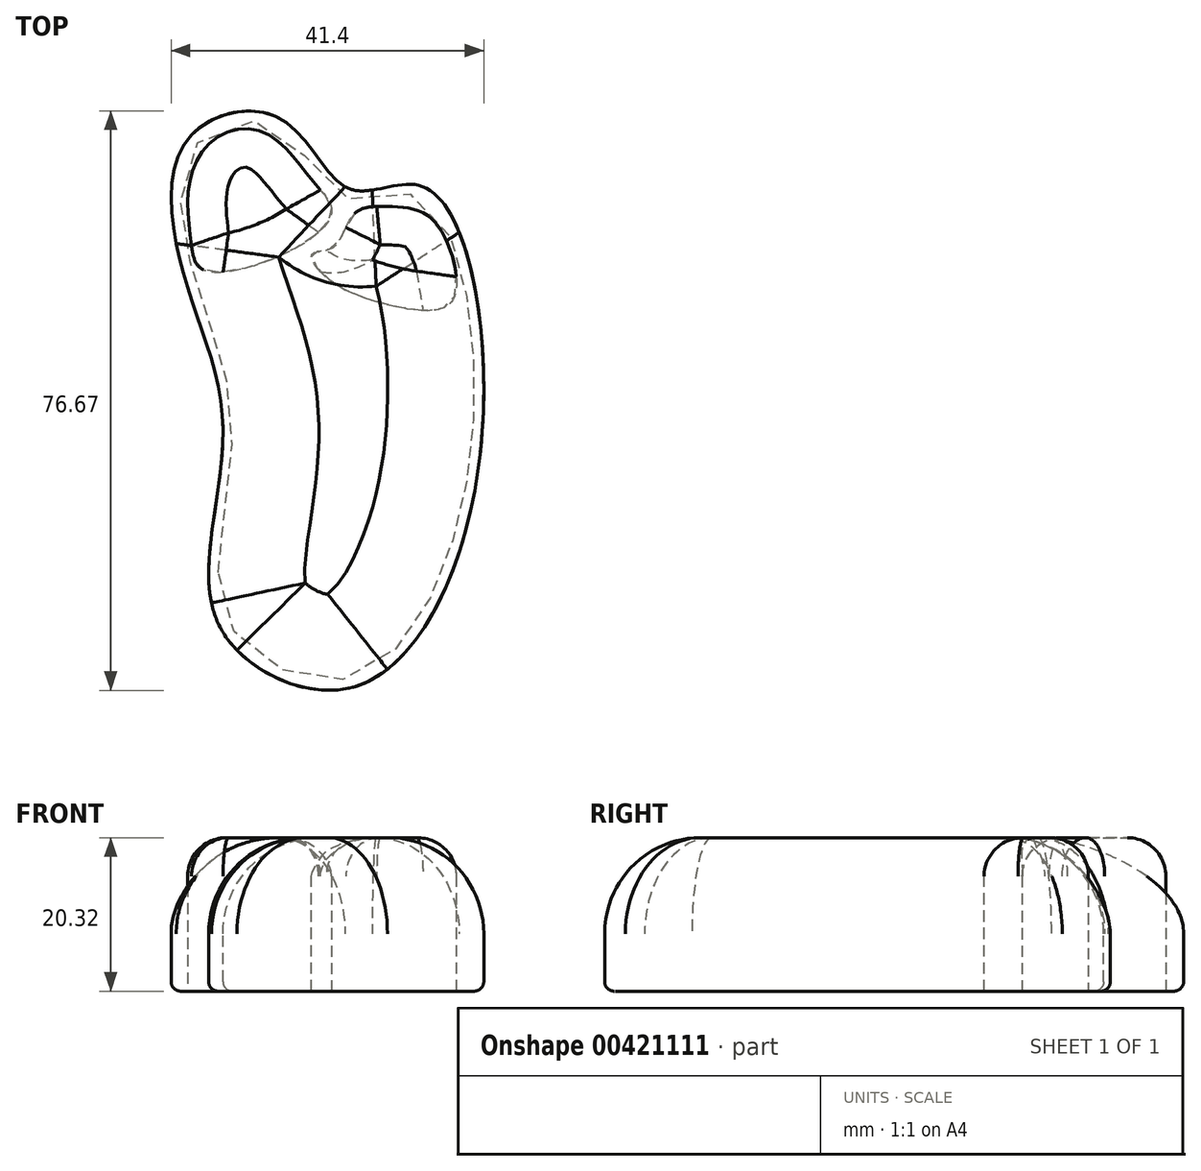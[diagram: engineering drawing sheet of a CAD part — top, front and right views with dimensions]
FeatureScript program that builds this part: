
annotation { "Feature Type Name" : "Feature", "Feature Type Description" : "" }
export const myFeature = defineFeature(function(context is Context, id is Id, definition is map)
    precondition{}
    {
        {
            var Q0;
            Q0=qCreatedBy(makeId("Top.planeOp"),FACE);
            var sketch = newSketch(context, id + "F0", { "sketchPlane" : qUnion([Q0])});
            skFitSpline(sketch, "E0", {"points": [v(-13.72, -25.12) * mm, v(-9.37, -36.03) * mm, v(6.49, -40) * mm, v(22.33, -8.6) * mm, v(14.89, 25.82) * mm, v(5.04, 25.58) * mm, v(-4.19, 34.89) * mm, v(-16.57, 32.07) * mm, v(-16.98, 14.19) * mm, v(-11.86, -4.88) * mm, v(-13.72, -25.12) * mm]});
            skSolve(sketch);
        }
        {
            var Q0;
            Q0=makeQuery(id+"F0.imprint","IMPRINT",FACE,{"disambiguationData":[TD([[makeQuery(id+"F0.imprint","IMPRINT",EDGE,{"derivedFrom":sQuery(id+"F0.wireOp",EDGE,"E0")}),1.0]])]});
            extrude(context, id + "F1", {"entities" : qUnion([Q0]), "depth" : 20.32 * mm});
        }
        {
            var Q0;
            Q0=makeQuery(id+"F1.opExtrude","CAP_EDGE",EDGE,{"disambiguationData":[OSD([sQuery(id+"F0.wireOp",EDGE,"E0")])],"isStart":false});
            fillet(context, id + "F2", {"entities" : qUnion([Q0]), "radius" : 12.7 * mm, "tangentPropagation" : true, "allowEdgeOverflow" : false});
        }
        {
            var Q0;
            Q0=makeQuery(id+"F1.opExtrude","CAP_EDGE",EDGE,{"disambiguationData":[OSD([sQuery(id+"F0.wireOp",EDGE,"E0")])],"isStart":true});
            fillet(context, id + "F3", {"entities" : qUnion([Q0]), "radius" : 1.27 * mm, "tangentPropagation" : true, "allowEdgeOverflow" : false});
        }
        {
            var Q0;
            Q0=qCreatedBy(makeId("Top.planeOp"),FACE);
            var sketch = newSketch(context, id + "F4", { "sketchPlane" : qUnion([Q0])});
            skFitSpline(sketch, "E1", {"points": [v(-14.42, 14.89) * mm, v(-16.05, 18.6) * mm, v(-16.28, 26.28) * mm, v(-12.8, 32.33) * mm, v(-6.28, 33.03) * mm, v(0, 26.75) * mm, v(2.56, 22.56) * mm, v(-3.26, 17.21) * mm, v(-14.42, 14.89) * mm]});
            skFitSpline(sketch, "E2", {"points": [v(5.58, 22.33) * mm, v(2.8, 17.9) * mm, v(0, 16.98) * mm, v(2.1, 13.72) * mm, v(11.4, 10) * mm, v(18.6, 10.93) * mm, v(16.28, 21.17) * mm, v(10.7, 23.26) * mm, v(5.58, 22.33) * mm]});
            skSolve(sketch);
        }
        {
            var Q0;
            Q0 = qSketchRegion(id + "F4", true);
            var Q1;
            Q1=sQuery(id+"F4.wireOp",EDGE,"E1");
            var Q2;
            Q2=sQuery(id+"F4.wireOp",EDGE,"E2");
            extrude(context, id + "F5", {"entities" : qUnion([Q0]), "surfaceEntities" : qUnion([Q1, Q2]), "depth" : 20.32 * mm});
        }
        {
            var Q0;
            Q0=makeQuery(id+"F5.opExtrude","CAP_EDGE",EDGE,{"disambiguationData":[OSD([sQuery(id+"F4.wireOp",EDGE,"E2")])],"isStart":false});
            var Q1;
            Q1=makeQuery(id+"F5.opExtrude","CAP_EDGE",EDGE,{"disambiguationData":[OSD([sQuery(id+"F4.wireOp",EDGE,"E1")])],"isStart":false});
            fillet(context, id + "F6", {"entities" : qUnion([Q0, Q1]), "radius" : 5.08 * mm, "tangentPropagation" : true, "allowEdgeOverflow" : false});
        }
    });
